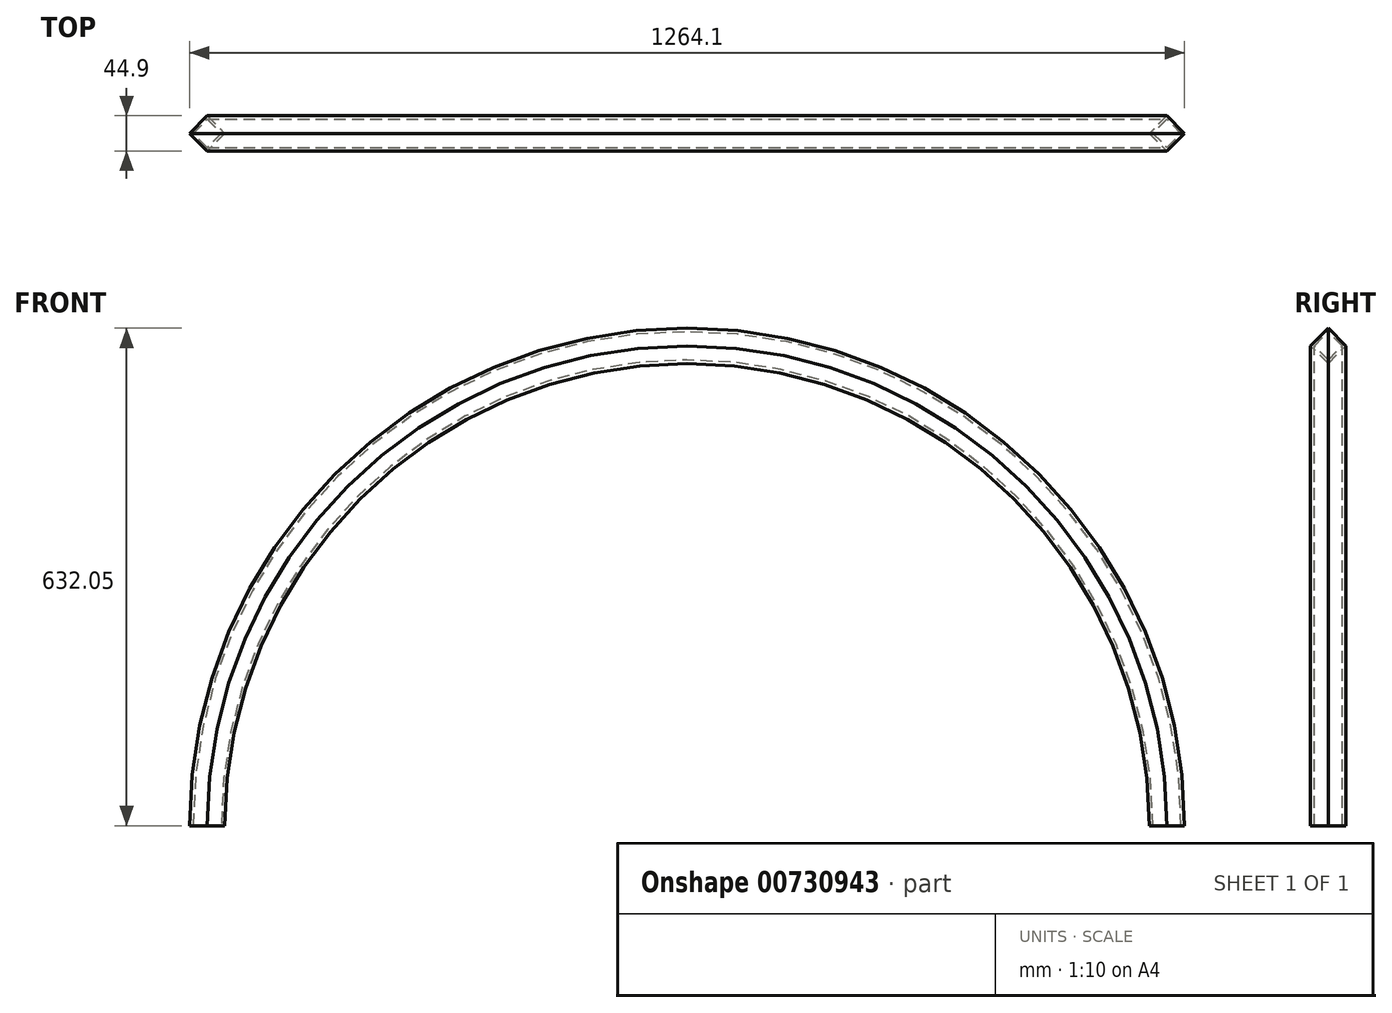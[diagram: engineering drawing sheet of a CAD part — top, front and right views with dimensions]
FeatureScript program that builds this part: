
annotation { "Feature Type Name" : "Feature", "Feature Type Description" : "" }
export const myFeature = defineFeature(function(context is Context, id is Id, definition is map)
    precondition{}
    {
        {
            var Q0;
            Q0=qCreatedBy(makeId("Front.planeOp"),FACE);
            var sketch = newSketch(context, id + "F0", { "sketchPlane" : qUnion([Q0])});
            skArc(sketch, "E0", {"start": v(609.6, 0) * mm, "mid": v(0, 609.6) * mm, "end": v(-609.6, 0) * mm});
            skSolve(sketch);
        }
        {
            var Q0;
            Q0=qCreatedBy(makeId("Top.planeOp"),FACE);
            var sketch = newSketch(context, id + "F1", { "sketchPlane" : qUnion([Q0])});
            skCircle(sketch, "E1.cCircle", {"center": v(-609.6, 0) * mm, "radius": 15.88 * mm, "construction": true});
            skLineSegment(sketch, "E1.0", {"start": v(-609.6, 22.45) * mm, "end": v(-587.15, 0) * mm});
            skLineSegment(sketch, "E1.1", {"start": v(-587.15, 0) * mm, "end": v(-609.6, -22.45) * mm});
            skLineSegment(sketch, "E1.2", {"start": v(-609.6, -22.45) * mm, "end": v(-632.05, 0) * mm});
            skLineSegment(sketch, "E1.3", {"start": v(-632.05, 0) * mm, "end": v(-609.6, 22.45) * mm});
            skPoint(sketch, "E1.0.midPoint", {"position": v(-598.37, 11.23) * mm});
            skCircle(sketch, "E2.cCircle", {"center": v(-609.6, 0) * mm, "radius": 12.7 * mm, "construction": true});
            skLineSegment(sketch, "E2.0", {"start": v(-609.6, -17.96) * mm, "end": v(-627.56, 0) * mm});
            skLineSegment(sketch, "E2.1", {"start": v(-627.56, 0) * mm, "end": v(-609.6, 17.96) * mm});
            skLineSegment(sketch, "E2.2", {"start": v(-609.6, 17.96) * mm, "end": v(-591.64, 0) * mm});
            skLineSegment(sketch, "E2.3", {"start": v(-591.64, 0) * mm, "end": v(-609.6, -17.96) * mm});
            skPoint(sketch, "E2.0.midPoint", {"position": v(-618.58, -8.98) * mm});
            skSolve(sketch);
        }
        {
            var Q0;
            Q0=makeQuery(id+"F1.imprint","IMPRINT",FACE,{"disambiguationData":[TD([[makeQuery(id+"F1.imprint","IMPRINT",EDGE,{"derivedFrom":sQuery(id+"F1.wireOp",EDGE,"E1.0")}),-1.0]])]});
            var Q1;
            Q1=sQuery(id+"F0.wireOp",EDGE,"E0");
            sweep(context, id + "F2", {"profiles" : qUnion([Q0]), "path" : qUnion([Q1])});
        }
    });
